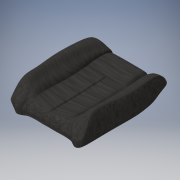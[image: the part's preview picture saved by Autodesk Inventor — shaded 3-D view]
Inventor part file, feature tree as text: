
AUTODESK INVENTOR PART (.ipt)
format: ipt  version: 2019 (Build 230136000, 136)  size: 1,313,792 bytes
history: native  units: in
note: dims shown in document units (in); Inventor stores cm internally (conversion verified against a paired STEP export)
features: sketch x11, plane x10, other x6, extrude x2, shell x1, hole x1, projected_geometry x1
ambient origin geometry x8: Origin, YZ Plane, XZ Plane, XY Plane, X Axis, Y Axis, Z Axis, Center Point
bodies: Solid7 (feature_tree)
feature tree (32):
  other  "Blocks"
  plane  "Work Plane2"
  plane  "Work Plane3"
  plane  "Work Plane4"
  plane  "Work Plane5"
  plane  "Work Plane6"
  plane  "Work Plane7"
  plane  "Work Plane8"
  sketch  "Sketch3"  dims[d22=7.0866in d23=1.9685in d24=0.9843in]
  sketch  "Sketch4"  dims[d25=3.1496in d26=-6.2992in]
  sketch  "Sketch5"  dims[d27=-3.937in d28=-11.811in]
  sketch  "Sketch6"  dims[d47=0.7874in]
  sketch  "Sketch7"  dims[d48=7.874in d49=0.0in]
  sketch  "Sketch8"  dims[d53=0.5906in]
  sketch  "Sketch9"  dims[d54=1.9685in]
  sketch  "Sketch10"  dims[d55=4.7244in]
  other  "Form3"
  plane  "Work Plane11"
  extrude  "Extrusion7"  Depth=1.9685in
  other  "Decal1"
  shell  "Shell1"  Thickness=0.9843in
  extrude  "Extrusion3"  [1 undecoded]
  plane  "Work Plane12"
  hole  "Hole1"  [1 undecoded]
  projected_geometry  "Projected Loop1"
  plane  "Work Plane10"
  sketch  "Sketch17"  dims[d76=0.0344in d77=3.937in]
  other  "Block1"
  sketch  "Sketch18"  dims[d78=0.7874in d79=0.0in]
  other  "Image2"
  sketch  "Sketch19"  dims[d94=0.0197in d95=-31.4961in d96=6.6929in d97=3.3465in d98=0.5906in d99=0.2362in d100=0.1575in d101=0.0787in d102=90.0deg d103=1.9685in d104=0.8108in d105=3.3858in d107=6.6929in d108=8.6614in d109=0.1969in d110=2.3622in]
  other  "Block1:1"
note: 2 required parameter values undecoded (feature->parameter linkage not recoverable at this tier; creation-order binding heuristic only, values carry confidence <= 0.55)
